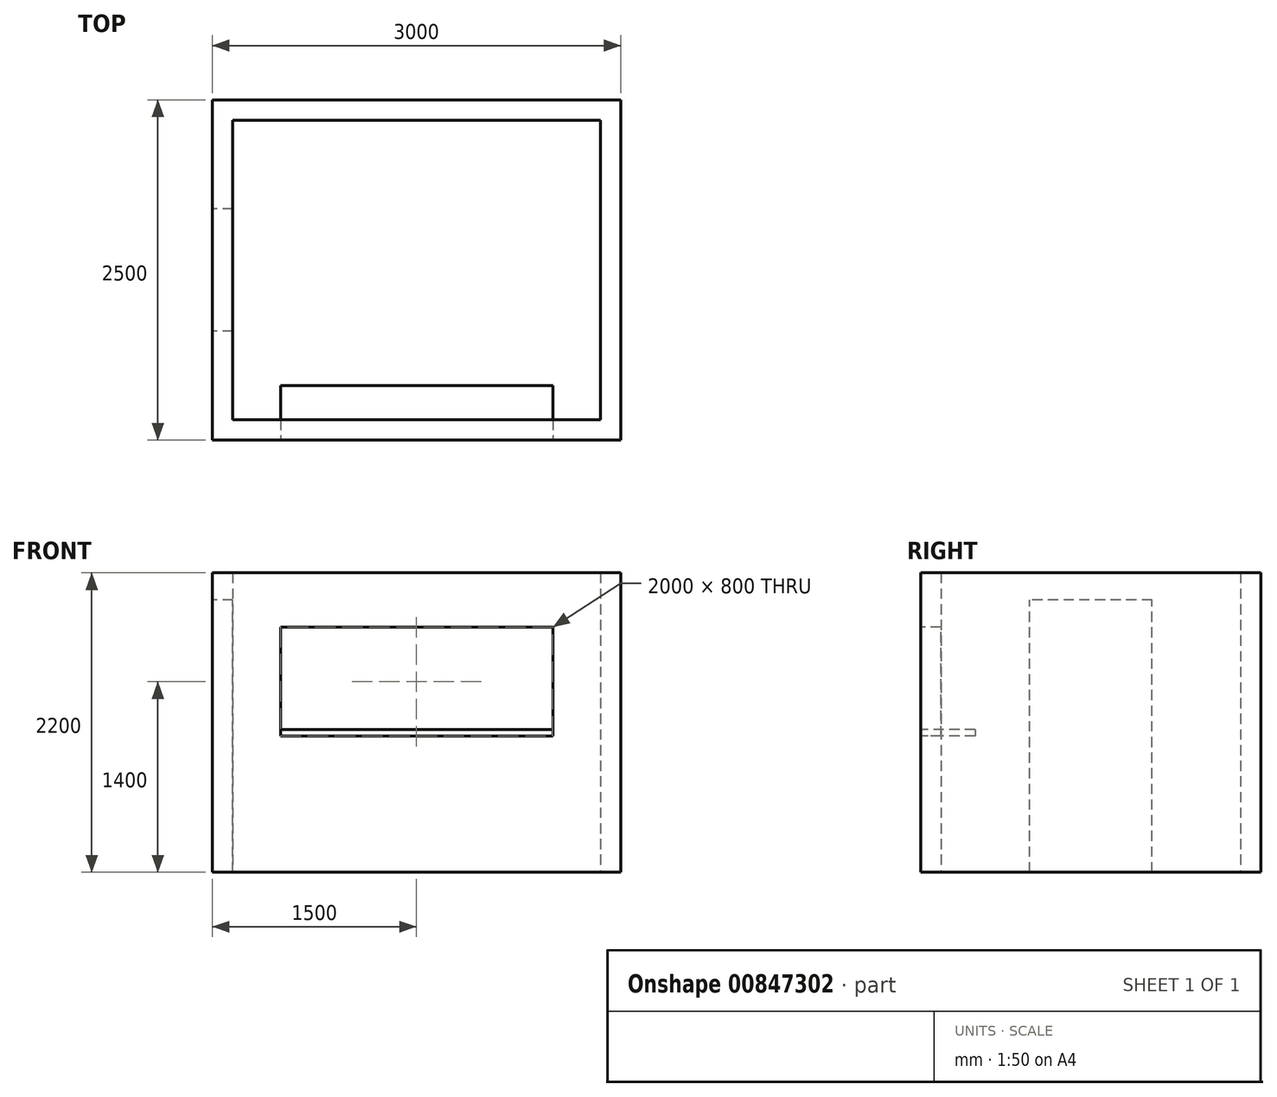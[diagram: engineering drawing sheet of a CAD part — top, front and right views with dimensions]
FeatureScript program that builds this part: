
annotation { "Feature Type Name" : "Feature", "Feature Type Description" : "" }
export const myFeature = defineFeature(function(context is Context, id is Id, definition is map)
    precondition{}
    {
        {
            var Q0;
            Q0=qCreatedBy(makeId("Top.planeOp"),FACE);
            var sketch = newSketch(context, id + "F0", { "sketchPlane" : qUnion([Q0])});
            skLineSegment(sketch, "E0.bottom", {"start": v(-1495.04, 1607.86) * mm, "end": v(1504.96, 1607.86) * mm});
            skLineSegment(sketch, "E0.top", {"start": v(-1495.04, -892.14) * mm, "end": v(1504.96, -892.14) * mm});
            skLineSegment(sketch, "E0.left", {"start": v(-1495.04, 1607.86) * mm, "end": v(-1495.04, -892.14) * mm});
            skLineSegment(sketch, "E0.right", {"start": v(1504.96, 1607.86) * mm, "end": v(1504.96, -892.14) * mm});
            skLineSegment(sketch, "E1.bottom", {"start": v(-1345.04, -742.14) * mm, "end": v(1354.96, -742.14) * mm});
            skLineSegment(sketch, "E1.top", {"start": v(-1345.04, 1457.86) * mm, "end": v(1354.96, 1457.86) * mm});
            skLineSegment(sketch, "E1.left", {"start": v(-1345.04, -742.14) * mm, "end": v(-1345.04, 1457.86) * mm});
            skLineSegment(sketch, "E1.right", {"start": v(1354.96, -742.14) * mm, "end": v(1354.96, 1457.86) * mm});
            skSolve(sketch);
        }
        {
            var Q0;
            Q0 = qSketchRegion(id + "F0", true);
            extrude(context, id + "F1", {"entities" : qUnion([Q0]), "depth" : 2200 * mm, "offsetDistance" : 25 * mm});
        }
        {
            var Q0;
            Q0 = qSketchRegion(id + "F0", true);
            extrude(context, id + "F2", {"entities" : qUnion([Q0]), "operationType" : NewBodyOperationType.ADD, "depth" : 2200 * mm, "offsetDistance" : 25 * mm});
        }
        {
            var Q0;
            Q0=makeQuery(id+"F1.opExtrude","SWEPT_FACE",FACE,{"disambiguationData":[OSD([sQuery(id+"F0.wireOp",EDGE,"E0.top")])]});
            var sketch = newSketch(context, id + "F3", { "sketchPlane" : qUnion([Q0])});
            skLineSegment(sketch, "E2.bottom", {"start": v(-995.04, 1800) * mm, "end": v(1004.96, 1800) * mm});
            skLineSegment(sketch, "E2.top", {"start": v(-995.04, 1000) * mm, "end": v(1004.96, 1000) * mm});
            skLineSegment(sketch, "E2.left", {"start": v(-995.04, 1800) * mm, "end": v(-995.04, 1000) * mm});
            skLineSegment(sketch, "E2.right", {"start": v(1004.96, 1800) * mm, "end": v(1004.96, 1000) * mm});
            skSolve(sketch);
        }
        {
            var Q0;
            Q0 = qSketchRegion(id + "F3", true);
            extrude(context, id + "F4", {"entities" : qUnion([Q0]), "operationType" : NewBodyOperationType.REMOVE, "oppositeDirection" : true, "depth" : 300 * mm, "offsetDistance" : 25 * mm});
        }
        {
            var Q0;
            Q0=makeQuery(id+"F1.opExtrude","SWEPT_FACE",FACE,{"disambiguationData":[OSD([sQuery(id+"F0.wireOp",EDGE,"E0.left")])]});
            var sketch = newSketch(context, id + "F5", { "sketchPlane" : qUnion([Q0])});
            skLineSegment(sketch, "E3.bottom", {"start": v(-807.86, 0) * mm, "end": v(92.14, 0) * mm});
            skLineSegment(sketch, "E3.top", {"start": v(-807.86, 2000) * mm, "end": v(92.14, 2000) * mm});
            skLineSegment(sketch, "E3.left", {"start": v(-807.86, 0) * mm, "end": v(-807.86, 2000) * mm});
            skLineSegment(sketch, "E3.right", {"start": v(92.14, 0) * mm, "end": v(92.14, 2000) * mm});
            skSolve(sketch);
        }
        {
            var Q0;
            Q0 = qSketchRegion(id + "F5", true);
            extrude(context, id + "F6", {"entities" : qUnion([Q0]), "operationType" : NewBodyOperationType.REMOVE, "oppositeDirection" : true, "depth" : 300 * mm, "offsetDistance" : 25 * mm});
        }
        {
            var Q0;
            Q0=makeQuery(id+"F4.boolean.opBoolean","COPY",FACE,{"derivedFrom":makeQuery(id+"F4.opExtrude","SWEPT_FACE",FACE,{"disambiguationData":[OSD([sQuery(id+"F3.wireOp",EDGE,"E2.top")])]})});
            var sketch = newSketch(context, id + "F7", { "sketchPlane" : qUnion([Q0])});
            skLineSegment(sketch, "E4.bottom", {"start": v(-995.04, -492.14) * mm, "end": v(1004.96, -492.14) * mm});
            skLineSegment(sketch, "E4.top", {"start": v(-995.04, -892.14) * mm, "end": v(1004.96, -892.14) * mm});
            skLineSegment(sketch, "E4.left", {"start": v(-995.04, -492.14) * mm, "end": v(-995.04, -892.14) * mm});
            skLineSegment(sketch, "E4.right", {"start": v(1004.96, -492.14) * mm, "end": v(1004.96, -892.14) * mm});
            skSolve(sketch);
        }
        {
            var Q0;
            Q0 = qSketchRegion(id + "F7", true);
            extrude(context, id + "F8", {"entities" : qUnion([Q0]), "depth" : 50 * mm, "offsetDistance" : 25 * mm});
        }
    });
